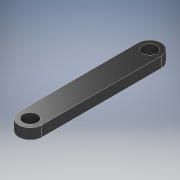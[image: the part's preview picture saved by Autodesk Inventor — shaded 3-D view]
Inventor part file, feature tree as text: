
AUTODESK INVENTOR PART (.ipt)
format: ipt  version: 2021 (Build 250183000, 183)  size: 109,056 bytes
history: native  units: mm
features: extrude x1, sketch x1
ambient origin geometry x8: Origin, YZ Plane, XZ Plane, XY Plane, X Axis, Y Axis, Z Axis, Center Point
bodies: Solid1 (feature_tree)
feature tree (2):
  extrude  "Extrusion1"  Depth=6.5mm
  sketch  "Sketch1"  dims[d0=33.75mm d1=6.5mm d2=4.0mm d3=4.0mm d4=3.0mm d5=0.0mm]
